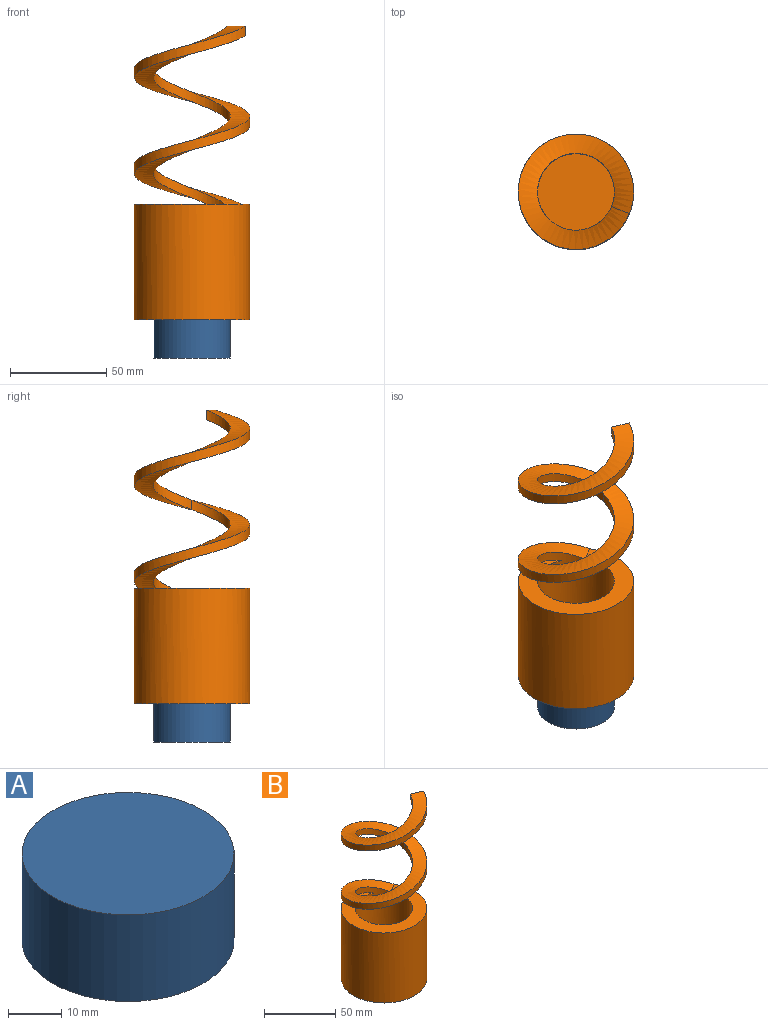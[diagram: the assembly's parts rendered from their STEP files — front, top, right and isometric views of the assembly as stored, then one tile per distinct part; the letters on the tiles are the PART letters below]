
ASSEMBLY  parts=2 mates=1
PART A: 3 faces, bbox 40x40x20 mm
  f0: cylinder r=20mm len=40mm, axis (0,0,-1), area 2513.3mm2, adj f1,f2
  f1: plane 40x40mm, normal (0,0,1), area 1256.6mm2, adj f0
  f2: plane 40x40mm, normal (0,0,-1), area 1256.6mm2, adj f0
PART B: 10 faces, bbox 61.6x61.6x152.5 mm
  f0: plane 9.24x5mm, normal (0.38,0.92,0), area 50mm2, adj f1,f3,f4,f5
  f1: bspline ~95.83x61.59mm, area 3052.1mm2, adj f0,f2,f3,f5,f6,f7
  f2: cylinder r=30mm len=105.63mm, axis (0,0,1), area 12123.4mm2, adj f1,f3,f4,f7,f8
  f3: cylinder r=30mm len=60mm, axis (0,0,1), area 883.6mm2, adj f0,f1,f2,f4
  f4: bspline ~91.67x61.59mm, area 2886.8mm2, adj f0,f2,f3,f5,f6,f7
  f5: cylinder r=20mm len=51.87mm, axis (0,0,1), area 589mm2, adj f0,f1,f4,f6
  f6: cylinder r=20mm len=95.63mm, axis (0,0,1), area 6825.7mm2, adj f1,f4,f5,f7,f9
  f7: plane 60x60mm, normal (0,0,1), area 1413.4mm2, adj f1,f2,f4,f6
  f8: plane 60x60mm, normal (0,0,-1), area 2827.4mm2, adj f2
  f9: plane 40x40mm, normal (0,0,1), area 1256.6mm2, adj f6
PLACE A at identity fixed
PLACE B at identity
MATE fastened B.f2 <-> A.f0  axis (0,0,-1) through (0,0,20)mm
